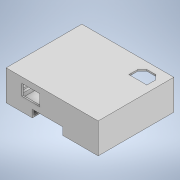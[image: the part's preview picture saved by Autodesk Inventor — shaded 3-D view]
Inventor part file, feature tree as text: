
AUTODESK INVENTOR PART (.ipt)
format: ipt  version: 2022 (Build 260153000, 153)  size: 301,056 bytes
history: native  units: in
note: dims shown in document units (in); Inventor stores cm internally (conversion verified against a paired STEP export)
features: extrude x13, sketch x12
ambient origin geometry x8: Origin, YZ Plane, XZ Plane, XY Plane, X Axis, Y Axis, Z Axis, Center Point
bodies: Solid1 (feature_tree)
feature tree (25):
  sketch  "Sketch1"  dims[d0=2.2047in d1=1.9685in]
  extrude  "Extrusion1"  Depth=1.9685in
  extrude  "Extrusion2"  Depth=0.0079in
  extrude  "Extrusion3"  TaperAngle=0.0deg  [1 undecoded]
  extrude  "Extrusion5"  Depth=0.0984in
  extrude  "Extrusion6"  Depth=0.0984in
  extrude  "Extrusion7"  Depth=0.0394in TaperAngle=0.0deg
  extrude  "Extrusion8"  Depth=0.0984in
  extrude  "Extrusion9"  Depth=0.0394in
  extrude  "Extrusion10"  TaperAngle=0.0deg  [1 undecoded]
  extrude  "Extrusion11"  Depth=0.0394in
  extrude  "Extrusion12"  TaperAngle=0.0deg  [1 undecoded]
  extrude  "Extrusion13"  Depth=0.8268in
  extrude  "Extrusion14"  TaperAngle=0.0deg  [1 undecoded]
  sketch  "Sketch2"  dims[d2=0.0079in d3=0.0079in]
  sketch  "Sketch3"  dims[d4=0.0in d5=0.0in]
  sketch  "Sketch4"  dims[d6=0.0984in d7=0.0984in]
  sketch  "Sketch5"  dims[d8=0.0984in d9=0.0984in]
  sketch  "Sketch6"  dims[d10=0.5984in d11=0.0in d12=0.0394in d13=0.0in]
  sketch  "Sketch7"  dims[d14=0.0in d16=0.0984in]
  sketch  "Sketch8"  dims[d17=0.0394in d18=0.0394in]
  sketch  "Sketch9"  dims[d19=0.0in d20=0.0in]
  sketch  "Sketch10"  dims[d21=0.0669in d22=0.0394in]
  sketch  "Sketch11"  dims[d23=0.0984in d24=0.0in]
  sketch  "Sketch12"  dims[d25=0.5906in d26=0.8268in d27=0.0in d30=0.1969in d31=2.9813in d32=0.0in d33=0.2953in d34=0.4331in d35=0.7087in d36=0.3543in d37=2.9813in d38=0.0in d39=0.1181in d40=0.0in d41=1.4173in d42=1.6535in d43=0.0787in d44=0.5512in d45=0.1181in d46=0.1181in d47=45.0deg d48=135.0deg d49=0.1181in d50=0.0394in d51=0.0in d52=0.0394in d53=0.0394in d54=0.0394in d55=0.0394in d56=0.3937in d57=0.0in d58=0.1181in d59=0.3937in d60=0.0in d61=0.0394in d62=0.0in d63=0.0394in d64=0.0394in d65=0.0in d66=0.0591in d67=0.9813in d68=0.0in d69=0.0787in d70=0.0787in d71=0.0787in d73=0.0394in d74=0.9813in d75=0.0in]
note: 4 required parameter values undecoded (feature->parameter linkage not recoverable at this tier; creation-order binding heuristic only, values carry confidence <= 0.55)
